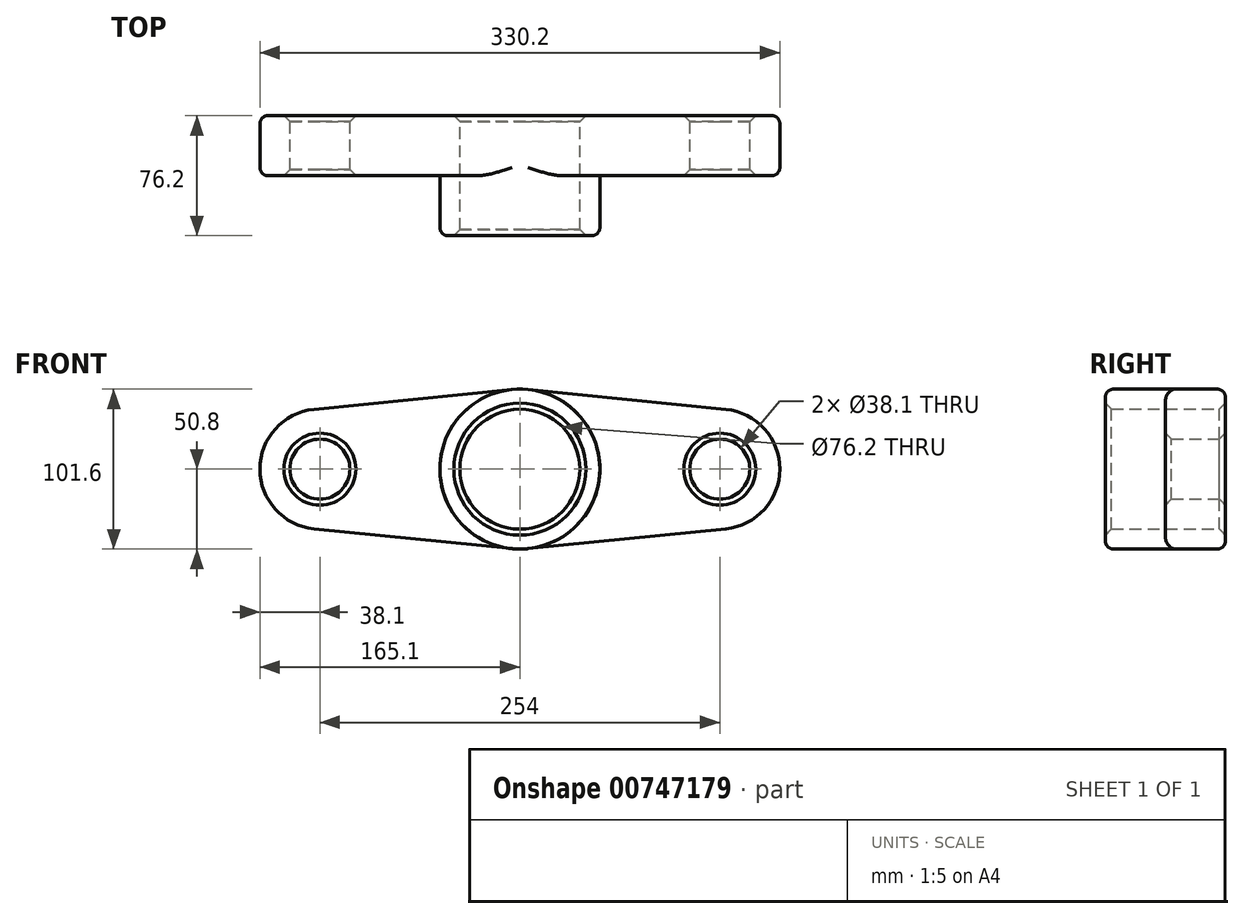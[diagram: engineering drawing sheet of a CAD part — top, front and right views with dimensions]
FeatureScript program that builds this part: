
annotation { "Feature Type Name" : "Feature", "Feature Type Description" : "" }
export const myFeature = defineFeature(function(context is Context, id is Id, definition is map)
    precondition{}
    {
        {
            var Q0;
            Q0=qCreatedBy(makeId("Front.planeOp"),FACE);
            var sketch = newSketch(context, id + "F0", { "sketchPlane" : qUnion([Q0])});
            skCircle(sketch, "E0", {"center": v(0, 0) * mm, "radius": 50.8 * mm});
            skCircle(sketch, "E1", {"center": v(127, 0) * mm, "radius": 38.1 * mm});
            skLineSegment(sketch, "E2", {"start": v(5.08, 50.55) * mm, "end": v(130.8, 37.9) * mm});
            skLineSegment(sketch, "E3", {"start": v(5.08, -50.55) * mm, "end": v(130.81, -37.9) * mm});
            skCircle(sketch, "E4", {"center": v(0, 0) * mm, "radius": 38.1 * mm});
            skCircle(sketch, "E5", {"center": v(127, 0) * mm, "radius": 19.05 * mm});
            skSolve(sketch);
        }
        {
            var Q0;
            Q0 = qSketchRegion(id + "F0", true);
            extrude(context, id + "F1", {"entities" : qUnion([Q0]), "depth" : 38.1 * mm, "offsetDistance" : 25.4 * mm});
        }
        {
            var Q0;
            Q0=makeQuery(id+"F0.imprint","IMPRINT",FACE,{"disambiguationData":[TD([[makeQuery(id+"F0.imprint","IMPRINT",EDGE,{"derivedFrom":sQuery(id+"F0.wireOp",EDGE,"E4")}),-1.0]])]});
            extrude(context, id + "F2", {"entities" : qUnion([Q0]), "operationType" : NewBodyOperationType.ADD, "depth" : 76.2 * mm, "offsetDistance" : 25.4 * mm});
        }
        {
            var Q0;
            Q0=makeQuery(id+"F2.opExtrude","CAP_EDGE",EDGE,{"disambiguationData":[OSD([sQuery(id+"F0.wireOp",EDGE,"E0")])],"isStart":false});
            var Q1;
            Q1=makeQuery(id+"F1.opExtrude","CAP_EDGE",EDGE,{"disambiguationData":[OSD([sQuery(id+"F0.wireOp",EDGE,"E3")])],"isStart":true});
            var Q2;
            Q2=makeQuery(id+"F1.opExtrude","CAP_EDGE",EDGE,{"disambiguationData":[OSD([sQuery(id+"F0.wireOp",EDGE,"E0")])],"isStart":true});
            var Q3;
            Q3=makeQuery(id+"F1.opExtrude","CAP_EDGE",EDGE,{"disambiguationData":[OSD([sQuery(id+"F0.wireOp",EDGE,"E2")])],"isStart":true});
            var Q4;
            Q4=makeQuery(id+"F1.opExtrude","CAP_EDGE",EDGE,{"disambiguationData":[OSD([sQuery(id+"F0.wireOp",EDGE,"E1")])],"isStart":true});
            fillet(context, id + "F3", {"entities" : qUnion([Q0, Q1, Q2, Q3, Q4]), "radius" : 5.08 * mm, "tangentPropagation" : true, "allowEdgeOverflow" : false});
        }
        {
            var Q0;
            Q0=makeQuery(id+"F1.opExtrude","CAP_EDGE",EDGE,{"disambiguationData":[OSD([sQuery(id+"F0.wireOp",EDGE,"E3")])],"isStart":false});
            var Q1;
            Q1=makeQuery(id+"F1.opExtrude","CAP_EDGE",EDGE,{"disambiguationData":[OSD([sQuery(id+"F0.wireOp",EDGE,"E1")])],"isStart":false});
            var Q2;
            Q2=makeQuery(id+"F1.opExtrude","CAP_EDGE",EDGE,{"disambiguationData":[OSD([sQuery(id+"F0.wireOp",EDGE,"E2")])],"isStart":false});
            fillet(context, id + "F4", {"entities" : qUnion([Q0, Q1, Q2]), "radius" : 5.08 * mm, "tangentPropagation" : true, "allowEdgeOverflow" : false});
        }
        {
            var Q0;
            Q0=makeQuery(id+"F2.opExtrude","CAP_EDGE",EDGE,{"disambiguationData":[OSD([sQuery(id+"F0.wireOp",EDGE,"E4")])],"isStart":false});
            chamfer(context, id + "F5", {"entities" : qUnion([Q0]), "width" : 3.8 * mm, "tangentPropagation" : true});
        }
        {
            var Q0;
            Q0=makeQuery(id+"F1.opExtrude","CAP_EDGE",EDGE,{"disambiguationData":[OSD([sQuery(id+"F0.wireOp",EDGE,"E4")])],"isStart":true});
            var Q1;
            Q1=makeQuery(id+"F1.opExtrude","CAP_EDGE",EDGE,{"disambiguationData":[OSD([sQuery(id+"F0.wireOp",EDGE,"E5")])],"isStart":true});
            var Q2;
            Q2=makeQuery(id+"F1.opExtrude","CAP_EDGE",EDGE,{"disambiguationData":[OSD([sQuery(id+"F0.wireOp",EDGE,"E5")])],"isStart":false});
            chamfer(context, id + "F6", {"entities" : qUnion([Q0, Q1, Q2]), "width" : 3.8 * mm, "tangentPropagation" : true});
        }
        {
            var Q0;
            Q0=makeQuery(id+"F1.opExtrude","SWEPT_BODY",BODY,{"disambiguationData":[OSD([sQuery(id+"F0.wireOp",EDGE,"E0"),sQuery(id+"F0.wireOp",EDGE,"E1"),sQuery(id+"F0.wireOp",EDGE,"E2"),sQuery(id+"F0.wireOp",EDGE,"E3"),sQuery(id+"F0.wireOp",EDGE,"E4"),sQuery(id+"F0.wireOp",EDGE,"E5")])]});
            var Q1;
            Q1=qCreatedBy(makeId("Right.planeOp"),FACE);
            mirror(context, id + "F7", {"operationType" : NewBodyOperationType.ADD, "entities" : qUnion([Q0]), "mirrorPlane" : qUnion([Q1])});
        }
    });
